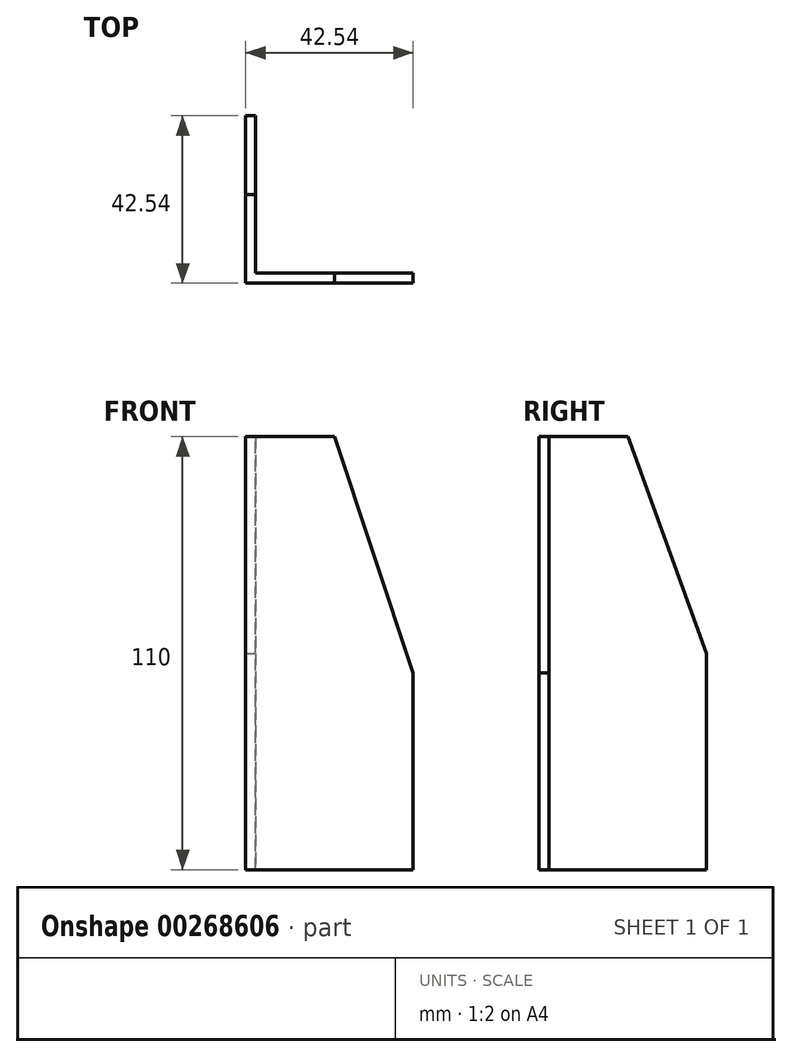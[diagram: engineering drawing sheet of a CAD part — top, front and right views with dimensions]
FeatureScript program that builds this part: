
annotation { "Feature Type Name" : "Feature", "Feature Type Description" : "" }
export const myFeature = defineFeature(function(context is Context, id is Id, definition is map)
    precondition{}
    {
        {
            var Q0;
            Q0=qCreatedBy(makeId("Front.planeOp"),FACE);
            var sketch = newSketch(context, id + "F0", { "sketchPlane" : qUnion([Q0])});
            skLineSegment(sketch, "E0.bottom", {"start": v(20, -25) * mm, "end": v(-20, -25) * mm});
            skLineSegment(sketch, "E0.left", {"start": v(20, -25) * mm, "end": v(20, 25) * mm});
            skLineSegment(sketch, "E0.right", {"start": v(-20, -25) * mm, "end": v(-20, 25) * mm});
            skPoint(sketch, "E0.middle", {"position": v(0, 0) * mm});
            skLineSegment(sketch, "E1", {"start": v(-20, 25) * mm, "end": v(-20, 85) * mm});
            skLineSegment(sketch, "E2", {"start": v(-20, 85) * mm, "end": v(0, 85) * mm});
            skLineSegment(sketch, "E3", {"start": v(0, 85) * mm, "end": v(20, 25) * mm});
            skSolve(sketch);
        }
        {
            var Q0;
            Q0=makeQuery(id+"F0.imprint","IMPRINT",FACE,{"disambiguationData":[TD([[makeQuery(id+"F0.imprint","IMPRINT",EDGE,{"derivedFrom":sQuery(id+"F0.wireOp",EDGE,"E0.bottom")}),-1.0]])]});
            extrude(context, id + "F1", {"entities" : qUnion([Q0]), "depth" : 2.54 * mm});
        }
        {
            var Q0;
            Q0=makeQuery(id+"F1.opExtrude","SWEPT_FACE",FACE,{"disambiguationData":[OSD([sQuery(id+"F0.wireOp",EDGE,"E0.right"),sQuery(id+"F0.wireOp",EDGE,"E1")])]});
            var sketch = newSketch(context, id + "F2", { "sketchPlane" : qUnion([Q0])});
            skLineSegment(sketch, "E4", {"start": v(2.54, -25) * mm, "end": v(-40, -25) * mm});
            skLineSegment(sketch, "E5", {"start": v(-40, 30) * mm, "end": v(-40, -25) * mm});
            skLineSegment(sketch, "E6", {"start": v(0, 85) * mm, "end": v(-20, 85) * mm});
            skLineSegment(sketch, "E7", {"start": v(-20, 85) * mm, "end": v(-40, 30) * mm});
            skLineSegment(sketch, "E8", {"start": v(0, 85) * mm, "end": v(2.54, 85) * mm});
            skLineSegment(sketch, "E9", {"start": v(2.54, 85) * mm, "end": v(2.54, -25) * mm});
            skSolve(sketch);
        }
        {
            var Q0;
            {var subQ0=sQuery(id+"F2.wireOp",EDGE,"E5");Q0=makeQuery(id+"F2.imprint","IMPRINT",FACE,{"disambiguationData":[TD([[makeQuery(id+"F2.imprint","IMPRINT",EDGE,{"derivedFrom":subQ0}),1.0]])]});}
            var Q1;
            Q1=makeQuery(id+"F2.imprint","IMPRINT",FACE,{"disambiguationData":[TD([[makeQuery(id+"F2.imprint","IMPRINT",EDGE,{"derivedFrom":sQuery(id+"F2.wireOp",EDGE,"E8")}),1.0]])]});
            extrude(context, id + "F3", {"entities" : qUnion([Q0, Q1]), "operationType" : NewBodyOperationType.ADD, "depth" : 2.54 * mm});
        }
    });
